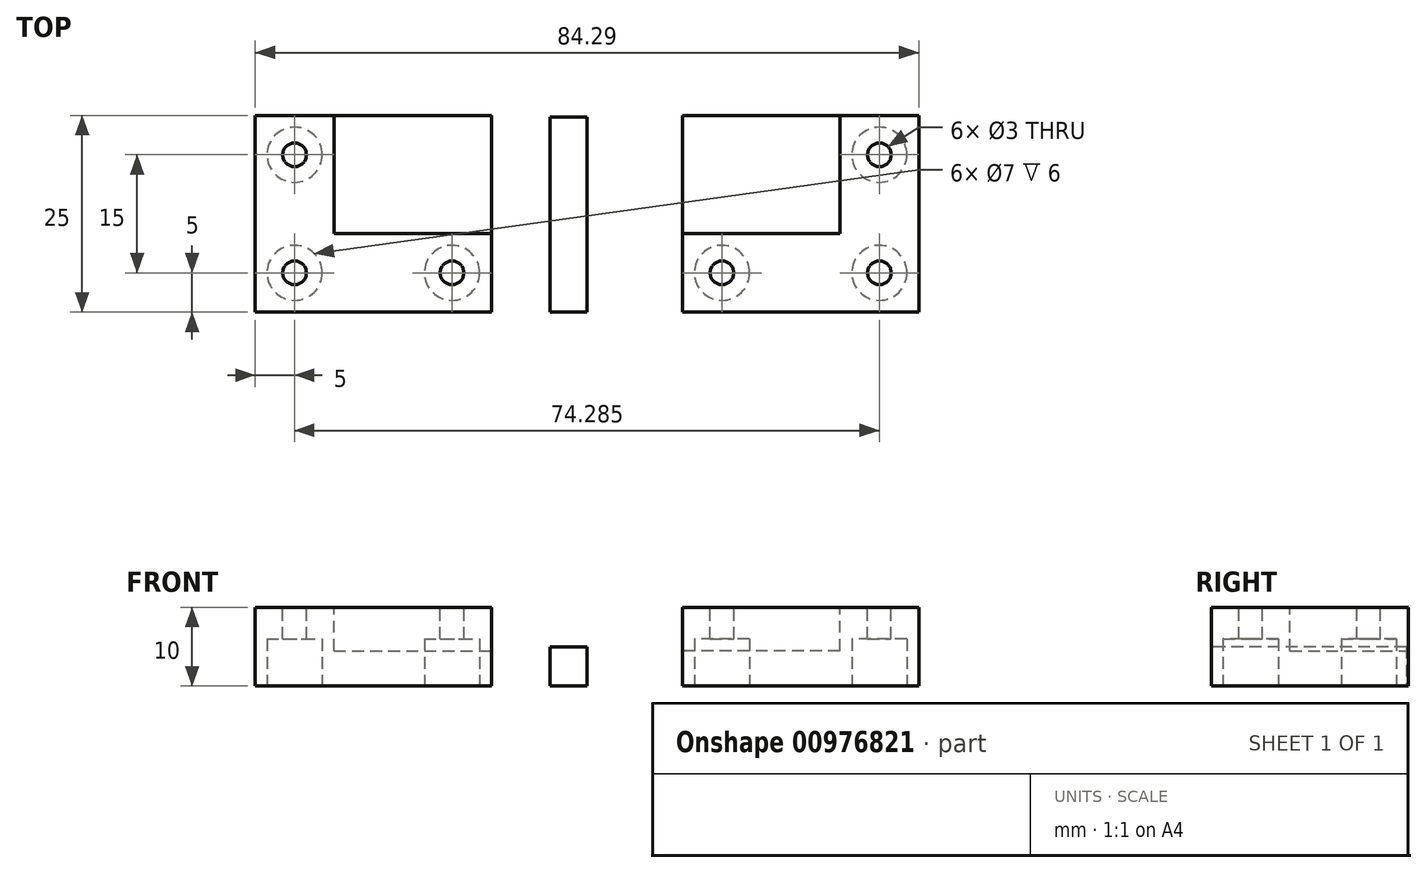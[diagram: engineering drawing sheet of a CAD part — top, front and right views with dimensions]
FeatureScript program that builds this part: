
annotation { "Feature Type Name" : "Feature", "Feature Type Description" : "" }
export const myFeature = defineFeature(function(context is Context, id is Id, definition is map)
    precondition{}
    {
        {
            var Q0;
            Q0=qCreatedBy(makeId("Top.planeOp"),FACE);
            var sketch = newSketch(context, id + "F0", { "sketchPlane" : qUnion([Q0])});
            skLineSegment(sketch, "E0.bottom", {"start": v(-15, -12.5) * mm, "end": v(15, -12.5) * mm});
            skLineSegment(sketch, "E0.top", {"start": v(-15, 12.5) * mm, "end": v(15, 12.5) * mm});
            skLineSegment(sketch, "E0.left", {"start": v(-15, -12.5) * mm, "end": v(-15, 12.5) * mm});
            skLineSegment(sketch, "E0.right", {"start": v(15, -12.5) * mm, "end": v(15, 12.5) * mm});
            skPoint(sketch, "E0.middle", {"position": v(0, 0) * mm});
            skSolve(sketch);
        }
        {
            var Q0;
            Q0 = qSketchRegion(id + "F0", true);
            extrude(context, id + "F1", {"entities" : qUnion([Q0]), "depth" : 10 * mm, "offsetDistance" : 25 * mm});
        }
        {
            var Q0;
            Q0=makeQuery(id+"F1.opExtrude","CAP_FACE",FACE,{"disambiguationData":[OSD([sQuery(id+"F0.wireOp",EDGE,"E0.bottom"),sQuery(id+"F0.wireOp",EDGE,"E0.top"),sQuery(id+"F0.wireOp",EDGE,"E0.left"),sQuery(id+"F0.wireOp",EDGE,"E0.right")])],"isStart":false});
            var sketch = newSketch(context, id + "F2", { "sketchPlane" : qUnion([Q0])});
            skLineSegment(sketch, "E1.bottom", {"start": v(15, 12.5) * mm, "end": v(-5, 12.5) * mm});
            skLineSegment(sketch, "E1.top", {"start": v(15, -2.5) * mm, "end": v(-5, -2.5) * mm});
            skLineSegment(sketch, "E1.left", {"start": v(15, 12.5) * mm, "end": v(15, -2.5) * mm});
            skLineSegment(sketch, "E1.right", {"start": v(-5, 12.5) * mm, "end": v(-5, -2.5) * mm});
            skSolve(sketch);
        }
        {
            var Q0;
            Q0=makeQuery(id+"F2.imprint","IMPRINT",FACE,{"disambiguationData":[TD([[makeQuery(id+"F2.imprint","IMPRINT",EDGE,{"derivedFrom":sQuery(id+"F2.wireOp",EDGE,"E1.bottom")}),-1.0]])]});
            extrude(context, id + "F3", {"entities" : qUnion([Q0]), "operationType" : NewBodyOperationType.REMOVE, "oppositeDirection" : true, "depth" : 5.5 * mm, "offsetDistance" : 25 * mm});
        }
        {
            var Q0;
            Q0=makeQuery(id+"F1.opExtrude","CAP_FACE",FACE,{"disambiguationData":[OSD([sQuery(id+"F0.wireOp",EDGE,"E0.bottom"),sQuery(id+"F0.wireOp",EDGE,"E0.top"),sQuery(id+"F0.wireOp",EDGE,"E0.left"),sQuery(id+"F0.wireOp",EDGE,"E0.right")])],"isStart":false});
            var sketch = newSketch(context, id + "F4", { "sketchPlane" : qUnion([Q0])});
            skLineSegment(sketch, "E2", {"start": v(-10, 12.5) * mm, "end": v(-10, 7.5) * mm, "construction": true});
            skLineSegment(sketch, "E3", {"start": v(15, -7.5) * mm, "end": v(10, -7.5) * mm, "construction": true});
            skCircle(sketch, "E4", {"center": v(-10, 7.5) * mm, "radius": 1.5 * mm});
            skCircle(sketch, "E5", {"center": v(10, -7.5) * mm, "radius": 1.5 * mm});
            skCircle(sketch, "E6", {"center": v(-10, -7.5) * mm, "radius": 1.5 * mm});
            skSolve(sketch);
        }
        {
            var Q0;
            Q0 = qSketchRegion(id + "F4", true);
            extrude(context, id + "F5", {"entities" : qUnion([Q0]), "operationType" : NewBodyOperationType.REMOVE, "oppositeDirection" : true, "depth" : 25 * mm, "offsetDistance" : 25 * mm});
        }
        {
            var Q0;
            Q0=makeQuery(id+"F1.opExtrude","CAP_FACE",FACE,{"disambiguationData":[OSD([sQuery(id+"F0.wireOp",EDGE,"E0.bottom"),sQuery(id+"F0.wireOp",EDGE,"E0.top"),sQuery(id+"F0.wireOp",EDGE,"E0.left"),sQuery(id+"F0.wireOp",EDGE,"E0.right")])],"isStart":true});
            var sketch = newSketch(context, id + "F6", { "sketchPlane" : qUnion([Q0])});
            skCircle(sketch, "E7", {"center": v(-10, -7.5) * mm, "radius": 3.5 * mm});
            skCircle(sketch, "E8", {"center": v(-10, 7.5) * mm, "radius": 3.5 * mm});
            skCircle(sketch, "E9", {"center": v(10, 7.5) * mm, "radius": 3.5 * mm});
            skSolve(sketch);
        }
        {
            var Q0;
            Q0 = qSketchRegion(id + "F6", true);
            extrude(context, id + "F7", {"entities" : qUnion([Q0]), "operationType" : NewBodyOperationType.REMOVE, "oppositeDirection" : true, "depth" : 6 * mm, "offsetDistance" : 25 * mm});
        }
        {
            var Q0;
            Q0=makeQuery(id+"F1.opExtrude","CAP_FACE",FACE,{"disambiguationData":[OSD([sQuery(id+"F0.wireOp",EDGE,"E0.bottom"),sQuery(id+"F0.wireOp",EDGE,"E0.top"),sQuery(id+"F0.wireOp",EDGE,"E0.left"),sQuery(id+"F0.wireOp",EDGE,"E0.right")])],"isStart":true});
            var sketch = newSketch(context, id + "F8", { "sketchPlane" : qUnion([Q0])});
            skLineSegment(sketch, "E10", {"start": v(15, 0) * mm, "end": v(22.48, 0) * mm});
            skLineSegment(sketch, "E11", {"start": v(22.48, 0) * mm, "end": v(22.48, 12.5) * mm});
            skLineSegment(sketch, "E12.bottom", {"start": v(22.48, 12.5) * mm, "end": v(27.14, 12.5) * mm});
            skLineSegment(sketch, "E12.top", {"start": v(22.48, -12.26) * mm, "end": v(27.14, -12.26) * mm});
            skLineSegment(sketch, "E12.left", {"start": v(22.48, 12.5) * mm, "end": v(22.48, -12.26) * mm});
            skLineSegment(sketch, "E12.right", {"start": v(27.14, 12.5) * mm, "end": v(27.14, -12.26) * mm});
            skSolve(sketch);
        }
        {
            var Q0;
            Q0 = qSketchRegion(id + "F8", true);
            extrude(context, id + "F9", {"entities" : qUnion([Q0]), "depth" : -5 * mm, "offsetDistance" : 25 * mm});
        }
        {
            var Q0;
            Q0=makeQuery(id+"F1.opExtrude","SWEPT_BODY",BODY,{"disambiguationData":[OSD([sQuery(id+"F0.wireOp",EDGE,"E0.bottom"),sQuery(id+"F0.wireOp",EDGE,"E0.top"),sQuery(id+"F0.wireOp",EDGE,"E0.left"),sQuery(id+"F0.wireOp",EDGE,"E0.right")])]});
            var Q1;
            Q1=makeQuery(id+"F9.opExtrude","SWEPT_FACE",FACE,{"disambiguationData":[OSD([sQuery(id+"F8.wireOp",EDGE,"E12.right")])]});
            mirror(context, id + "F10", {"entities" : qUnion([Q0]), "mirrorPlane" : qUnion([Q1])});
        }
    });
